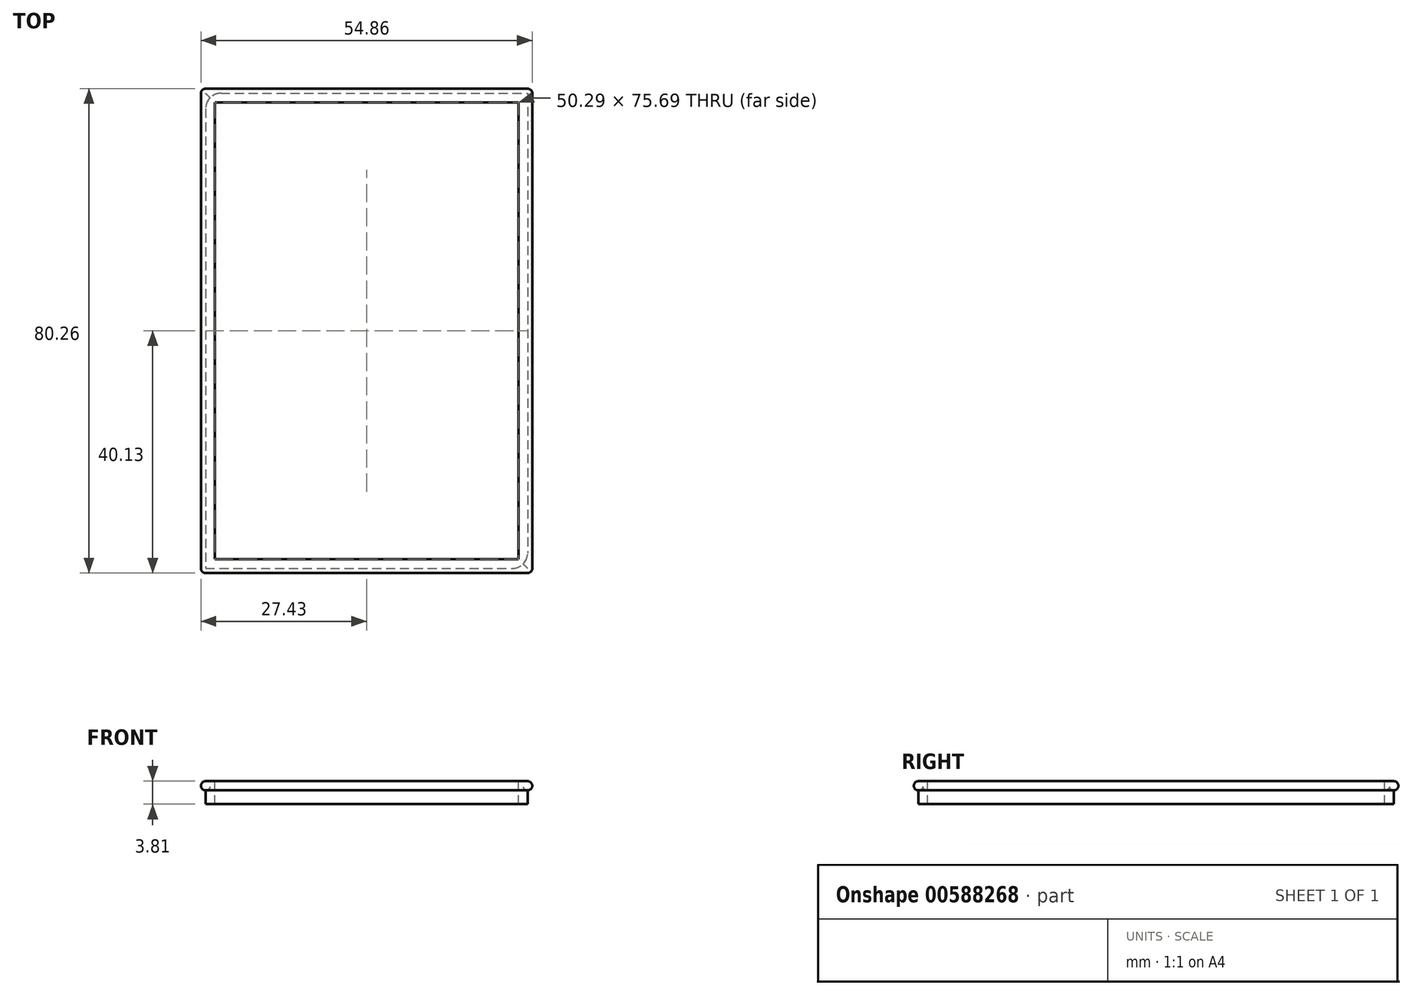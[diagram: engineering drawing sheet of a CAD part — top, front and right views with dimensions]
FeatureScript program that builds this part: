
annotation { "Feature Type Name" : "Feature", "Feature Type Description" : "" }
export const myFeature = defineFeature(function(context is Context, id is Id, definition is map)
    precondition{}
    {
        {
            var Q0;
            Q0=qCreatedBy(makeId("Front.planeOp"),FACE);
            var sketch = newSketch(context, id + "F0", { "sketchPlane" : qUnion([Q0])});
            skLineSegment(sketch, "E0.bottom", {"start": v(26.67, -20.32) * mm, "end": v(-26.67, -20.32) * mm});
            skLineSegment(sketch, "E0.top", {"start": v(26.67, 20.32) * mm, "end": v(-26.67, 20.32) * mm});
            skLineSegment(sketch, "E0.left", {"start": v(26.67, -20.32) * mm, "end": v(26.67, 20.32) * mm});
            skLineSegment(sketch, "E0.right", {"start": v(-26.67, -20.32) * mm, "end": v(-26.67, 20.32) * mm});
            skPoint(sketch, "E0.middle", {"position": v(0, 0) * mm});
            skSolve(sketch);
        }
        {
            var Q0;
            Q0=makeQuery(id+"F0.imprint","IMPRINT",FACE,{"disambiguationData":[TD([[makeQuery(id+"F0.imprint","IMPRINT",EDGE,{"derivedFrom":sQuery(id+"F0.wireOp",EDGE,"E0.bottom")}),-1.0]])]});
            extrude(context, id + "F1", {"entities" : qUnion([Q0]), "endBound" : BoundingType.SYMMETRIC, "depth" : 78.74 * mm});
        }
        {
            var Q0;
            Q0=makeQuery(id+"F1.opExtrude","SWEPT_FACE",FACE,{"disambiguationData":[OSD([sQuery(id+"F0.wireOp",EDGE,"E0.top")])]});
            shell(context, id + "F2", {"entities" : qUnion([Q0]), "thickness" : 1.52 * mm});
        }
        {
            var Q0;
            Q0=makeQuery(id+"F1.opExtrude","CAP_FACE",FACE,{"disambiguationData":[OSD([sQuery(id+"F0.wireOp",EDGE,"E0.bottom"),sQuery(id+"F0.wireOp",EDGE,"E0.top"),sQuery(id+"F0.wireOp",EDGE,"E0.left"),sQuery(id+"F0.wireOp",EDGE,"E0.right")])],"isStart":false});
            var sketch = newSketch(context, id + "F3", { "sketchPlane" : qUnion([Q0])});
            skArc(sketch, "E1", {"start": v(-26.67, 20.32) * mm, "mid": v(-27.43, 19.56) * mm, "end": v(-26.67, 18.8) * mm});
            skSolve(sketch);
        }
        {
            var Q0;
            {var subQ0=sQuery(id+"F3.wireOp",EDGE,"E1");Q0=makeQuery(id+"F3.imprint","IMPRINT",FACE,{"disambiguationData":[TD([[makeQuery(id+"F3.imprint","IMPRINT",EDGE,{"derivedFrom":subQ0}),1.0]])]});}
            var Q1;
            Q1=makeQuery(id+"F1.opExtrude","SWEPT_EDGE",EDGE,{"disambiguationData":[OSD([sQuery(id+"F0.wireOp",EDGE,"E0.top"),sQuery(id+"F0.wireOp",EDGE,"E0.right")])]});
            var Q2;
            Q2=makeQuery(id+"F1.opExtrude","CAP_EDGE",EDGE,{"disambiguationData":[OSD([sQuery(id+"F0.wireOp",EDGE,"E0.top")])],"isStart":true});
            var Q3;
            Q3=makeQuery(id+"F1.opExtrude","SWEPT_EDGE",EDGE,{"disambiguationData":[OSD([sQuery(id+"F0.wireOp",EDGE,"E0.top"),sQuery(id+"F0.wireOp",EDGE,"E0.left")])]});
            var Q4;
            Q4=makeQuery(id+"F1.opExtrude","CAP_EDGE",EDGE,{"disambiguationData":[OSD([sQuery(id+"F0.wireOp",EDGE,"E0.top")])],"isStart":false});
            sweep(context, id + "F4", {"operationType" : NewBodyOperationType.ADD, "profiles" : qUnion([Q0]), "path" : qUnion([Q1, Q2, Q3, Q4])});
        }
        {
            var Q0;
            Q0=makeQuery(id+"F1.opExtrude","SWEPT_FACE",FACE,{"disambiguationData":[OSD([sQuery(id+"F0.wireOp",EDGE,"E0.bottom")])]});
            var sketch = newSketch(context, id + "F5", { "sketchPlane" : qUnion([Q0])});
            skLineSegment(sketch, "E2.bottom", {"start": v(26.67, 39.37) * mm, "end": v(21.75, 39.37) * mm});
            skLineSegment(sketch, "E2.left", {"start": v(26.67, 39.37) * mm, "end": v(26.67, 34.45) * mm});
            skPoint(sketch, "E3.newPointA", {"position": v(20.32, 19.05) * mm});
            skArc(sketch, "E4", {"start": v(20.52, 37.78) * mm, "mid": v(22.18, 34.88) * mm, "end": v(25.08, 33.22) * mm});
            skPoint(sketch, "E5.visualSharp", {"position": v(20.32, 39.37) * mm});
            skArc(sketch, "E5.filletArc", {"start": v(21.75, 39.37) * mm, "mid": v(20.75, 38.88) * mm, "end": v(20.52, 37.78) * mm});
            skPoint(sketch, "E6.visualSharp", {"position": v(26.67, 33.02) * mm});
            skArc(sketch, "E6.filletArc", {"start": v(25.08, 33.22) * mm, "mid": v(26.18, 33.45) * mm, "end": v(26.67, 34.45) * mm});
            skArc(sketch, "E7.MirrorCS", {"start": v(-21.75, 39.37) * mm, "mid": v(-20.75, 38.88) * mm, "end": v(-20.52, 37.78) * mm});
            skArc(sketch, "E8.MirrorCS", {"start": v(-20.52, 37.78) * mm, "mid": v(-22.18, 34.88) * mm, "end": v(-25.08, 33.22) * mm});
            skArc(sketch, "E9.MirrorCS", {"start": v(-25.08, 33.22) * mm, "mid": v(-26.18, 33.45) * mm, "end": v(-26.67, 34.45) * mm});
            skLineSegment(sketch, "E10.MirrorCS", {"start": v(-26.67, 39.37) * mm, "end": v(-26.67, 34.45) * mm});
            skLineSegment(sketch, "E11.MirrorCS", {"start": v(-26.67, 39.37) * mm, "end": v(-21.75, 39.37) * mm});
            skArc(sketch, "E12.MirrorCS", {"start": v(-20.52, -37.78) * mm, "mid": v(-22.18, -34.88) * mm, "end": v(-25.08, -33.22) * mm});
            skArc(sketch, "E13.MirrorCS", {"start": v(-21.75, -39.37) * mm, "mid": v(-20.75, -38.88) * mm, "end": v(-20.52, -37.78) * mm});
            skLineSegment(sketch, "E14.MirrorCS", {"start": v(-26.67, -39.37) * mm, "end": v(-21.75, -39.37) * mm});
            skLineSegment(sketch, "E15.MirrorCS", {"start": v(-26.67, -39.37) * mm, "end": v(-26.67, -34.45) * mm});
            skArc(sketch, "E16.MirrorCS", {"start": v(-25.08, -33.22) * mm, "mid": v(-26.18, -33.45) * mm, "end": v(-26.67, -34.45) * mm});
            skArc(sketch, "E17.MirrorCS", {"start": v(21.75, -39.37) * mm, "mid": v(20.75, -38.88) * mm, "end": v(20.52, -37.78) * mm});
            skArc(sketch, "E18.MirrorCS", {"start": v(20.52, -37.78) * mm, "mid": v(22.18, -34.88) * mm, "end": v(25.08, -33.22) * mm});
            skArc(sketch, "E19.MirrorCS", {"start": v(25.08, -33.22) * mm, "mid": v(26.18, -33.45) * mm, "end": v(26.67, -34.45) * mm});
            skLineSegment(sketch, "E20.MirrorCS", {"start": v(26.67, -39.37) * mm, "end": v(26.67, -34.45) * mm});
            skLineSegment(sketch, "E21.MirrorCS", {"start": v(26.67, -39.37) * mm, "end": v(21.75, -39.37) * mm});
            skSolve(sketch);
        }
        {
            var Q0;
            Q0=makeQuery(id+"F5.imprint","IMPRINT",FACE,{"disambiguationData":[TD([[makeQuery(id+"F5.imprint","IMPRINT",EDGE,{"derivedFrom":sQuery(id+"F5.wireOp",EDGE,"E2.bottom")}),1.0]])]});
            var Q1;
            Q1=makeQuery(id+"F5.imprint","IMPRINT",FACE,{"disambiguationData":[TD([[makeQuery(id+"F5.imprint","IMPRINT",EDGE,{"derivedFrom":sQuery(id+"F5.wireOp",EDGE,"E8.MirrorCS")}),-1.0]])]});
            var Q2;
            Q2=makeQuery(id+"F5.imprint","IMPRINT",FACE,{"disambiguationData":[TD([[makeQuery(id+"F5.imprint","IMPRINT",EDGE,{"derivedFrom":sQuery(id+"F5.wireOp",EDGE,"E12.MirrorCS")}),1.0]])]});
            var Q3;
            Q3=makeQuery(id+"F5.imprint","IMPRINT",FACE,{"disambiguationData":[TD([[makeQuery(id+"F5.imprint","IMPRINT",EDGE,{"derivedFrom":sQuery(id+"F5.wireOp",EDGE,"E17.MirrorCS")}),-1.0]])]});
            extrude(context, id + "F6", {"entities" : qUnion([Q0, Q1, Q2, Q3]), "operationType" : NewBodyOperationType.ADD, "depth" : 2.8 * mm});
        }
        {
            var Q0;
            Q0=makeQuery(id+"F6.opExtrude","CAP_FACE",FACE,{"disambiguationData":[OSD([sQuery(id+"F5.wireOp",EDGE,"E2.bottom"),sQuery(id+"F5.wireOp",EDGE,"E2.left"),sQuery(id+"F5.wireOp",EDGE,"E4"),sQuery(id+"F5.wireOp",EDGE,"E5.filletArc"),sQuery(id+"F5.wireOp",EDGE,"E6.filletArc")])],"isStart":false});
            var Q1;
            Q1=makeQuery(id+"F6.opExtrude","CAP_FACE",FACE,{"disambiguationData":[OSD([sQuery(id+"F5.wireOp",EDGE,"E8.MirrorCS"),sQuery(id+"F5.wireOp",EDGE,"E9.MirrorCS"),sQuery(id+"F5.wireOp",EDGE,"E10.MirrorCS"),sQuery(id+"F5.wireOp",EDGE,"E7.MirrorCS"),sQuery(id+"F5.wireOp",EDGE,"E11.MirrorCS")])],"isStart":false});
            var Q2;
            Q2=makeQuery(id+"F6.opExtrude","CAP_FACE",FACE,{"disambiguationData":[OSD([sQuery(id+"F5.wireOp",EDGE,"E12.MirrorCS"),sQuery(id+"F5.wireOp",EDGE,"E13.MirrorCS"),sQuery(id+"F5.wireOp",EDGE,"E14.MirrorCS"),sQuery(id+"F5.wireOp",EDGE,"E15.MirrorCS"),sQuery(id+"F5.wireOp",EDGE,"E16.MirrorCS")])],"isStart":false});
            var Q3;
            Q3=makeQuery(id+"F6.opExtrude","CAP_FACE",FACE,{"disambiguationData":[OSD([sQuery(id+"F5.wireOp",EDGE,"E17.MirrorCS"),sQuery(id+"F5.wireOp",EDGE,"E18.MirrorCS"),sQuery(id+"F5.wireOp",EDGE,"E19.MirrorCS"),sQuery(id+"F5.wireOp",EDGE,"E20.MirrorCS"),sQuery(id+"F5.wireOp",EDGE,"E21.MirrorCS")])],"isStart":false});
            shell(context, id + "F7", {"entities" : qUnion([Q0, Q1, Q2, Q3]), "thickness" : 1.52 * mm});
        }
        {
            var Q0;
            Q0=makeQuery(id+"F2.opShell","OFFSET_FACE",FACE,{"disambiguationData":[OSD([sQuery(id+"F0.wireOp",EDGE,"E0.bottom")])]});
            fillet(context, id + "F8", {"entities" : qUnion([Q0]), "radius" : 0.76 * mm, "tangentPropagation" : true, "allowEdgeOverflow" : false});
        }
        {
            var Q0;
            Q0=makeQuery(id+"F1.opExtrude","SWEPT_EDGE",EDGE,{"disambiguationData":[OSD([sQuery(id+"F0.wireOp",EDGE,"E0.bottom"),sQuery(id+"F0.wireOp",EDGE,"E0.right")])]});
            var Q1;
            Q1=makeQuery(id+"F1.opExtrude","CAP_EDGE",EDGE,{"disambiguationData":[OSD([sQuery(id+"F0.wireOp",EDGE,"E0.bottom")])],"isStart":false});
            var Q2;
            Q2=makeQuery(id+"F1.opExtrude","SWEPT_EDGE",EDGE,{"disambiguationData":[OSD([sQuery(id+"F0.wireOp",EDGE,"E0.bottom"),sQuery(id+"F0.wireOp",EDGE,"E0.left")])]});
            var Q3;
            Q3=makeQuery(id+"F1.opExtrude","CAP_EDGE",EDGE,{"disambiguationData":[OSD([sQuery(id+"F0.wireOp",EDGE,"E0.bottom")])],"isStart":true});
            fillet(context, id + "F9", {"entities" : qUnion([Q0, Q1, Q2, Q3]), "radius" : 1.9 * mm, "tangentPropagation" : true, "allowEdgeOverflow" : false});
        }
        {
            var Q0;
            Q0=makeQuery(id+"F4.opSweep","MID_CAP_EDGE",EDGE,{"disambiguationData":[OSD([sQuery(id+"F0.wireOp",EDGE,"E0.top"),sQuery(id+"F0.wireOp",EDGE,"E0.left"),sQuery(id+"F3.wireOp",EDGE,"E1")])],"capPos":3.0});
            var Q1;
            Q1=makeQuery(id+"F4.opSweep","MID_CAP_EDGE",EDGE,{"disambiguationData":[OSD([sQuery(id+"F0.wireOp",EDGE,"E0.top"),sQuery(id+"F0.wireOp",EDGE,"E0.left"),sQuery(id+"F3.wireOp",EDGE,"E1")])],"capPos":2.0});
            var Q2;
            Q2=makeQuery(id+"F4.opSweep","MID_CAP_EDGE",EDGE,{"disambiguationData":[OSD([sQuery(id+"F0.wireOp",EDGE,"E0.top"),sQuery(id+"F0.wireOp",EDGE,"E0.right"),sQuery(id+"F3.wireOp",EDGE,"E1")])],"capPos":1.0});
            var Q3;
            Q3=makeQuery(id+"F4.opSweep","CAP_EDGE",EDGE,{"disambiguationData":[OSD([sQuery(id+"F0.wireOp",EDGE,"E0.top"),sQuery(id+"F0.wireOp",EDGE,"E0.right"),sQuery(id+"F3.wireOp",EDGE,"E1")])],"isStart":true});
            fillet(context, id + "F10", {"entities" : qUnion([Q0, Q1, Q2, Q3]), "radius" : 0.76 * mm, "tangentPropagation" : true, "allowEdgeOverflow" : false});
        }
        {
            var Q0;
            Q0=makeQuery(id+"F6.boolean.opBoolean","MERGE",EDGE,{"derivedFrom":[makeQuery(id+"F1.opExtrude","CAP_EDGE",EDGE,{"disambiguationData":[OSD([sQuery(id+"F0.wireOp",EDGE,"E0.left")])],"isStart":false}),makeQuery(id+"F6.opExtrude","SWEPT_EDGE",EDGE,{"disambiguationData":[OSD([sQuery(id+"F5.wireOp",EDGE,"E2.bottom"),sQuery(id+"F5.wireOp",EDGE,"E2.left")])]})]});
            var Q1;
            Q1=makeQuery(id+"F6.boolean.opBoolean","MERGE",EDGE,{"derivedFrom":[makeQuery(id+"F1.opExtrude","CAP_EDGE",EDGE,{"disambiguationData":[OSD([sQuery(id+"F0.wireOp",EDGE,"E0.left")])],"isStart":true}),makeQuery(id+"F6.opExtrude","SWEPT_EDGE",EDGE,{"disambiguationData":[OSD([sQuery(id+"F5.wireOp",EDGE,"E20.MirrorCS"),sQuery(id+"F5.wireOp",EDGE,"E21.MirrorCS")])]})]});
            var Q2;
            Q2=makeQuery(id+"F6.boolean.opBoolean","MERGE",EDGE,{"derivedFrom":[makeQuery(id+"F1.opExtrude","CAP_EDGE",EDGE,{"disambiguationData":[OSD([sQuery(id+"F0.wireOp",EDGE,"E0.right")])],"isStart":false}),makeQuery(id+"F6.opExtrude","SWEPT_EDGE",EDGE,{"disambiguationData":[OSD([sQuery(id+"F5.wireOp",EDGE,"E10.MirrorCS"),sQuery(id+"F5.wireOp",EDGE,"E11.MirrorCS")])]})]});
            var Q3;
            Q3=makeQuery(id+"F6.boolean.opBoolean","MERGE",EDGE,{"derivedFrom":[makeQuery(id+"F1.opExtrude","CAP_EDGE",EDGE,{"disambiguationData":[OSD([sQuery(id+"F0.wireOp",EDGE,"E0.right")])],"isStart":true}),makeQuery(id+"F6.opExtrude","SWEPT_EDGE",EDGE,{"disambiguationData":[OSD([sQuery(id+"F5.wireOp",EDGE,"E14.MirrorCS"),sQuery(id+"F5.wireOp",EDGE,"E15.MirrorCS")])]})]});
            fillet(context, id + "F11", {"entities" : qUnion([Q0, Q1, Q2, Q3]), "radius" : 2.54 * mm, "tangentPropagation" : true, "allowEdgeOverflow" : false});
        }
        {
            var Q0;
            Q0=makeQuery(id+"F1.opExtrude","SWEPT_BODY",BODY,{"disambiguationData":[OSD([sQuery(id+"F0.wireOp",EDGE,"E0.bottom"),sQuery(id+"F0.wireOp",EDGE,"E0.top"),sQuery(id+"F0.wireOp",EDGE,"E0.left"),sQuery(id+"F0.wireOp",EDGE,"E0.right")])]});
            transform(context, id + "F12", {"entities" : qUnion([Q0]), "transformType" : TransformType.COPY});
        }
        {
            var Q0;
            Q0=makeQuery(id+"F12.opPattern","COPY",BODY,{"derivedFrom":makeQuery(id+"F1.opExtrude","SWEPT_BODY",BODY,{"disambiguationData":[OSD([sQuery(id+"F0.wireOp",EDGE,"E0.bottom"),sQuery(id+"F0.wireOp",EDGE,"E0.top"),sQuery(id+"F0.wireOp",EDGE,"E0.left"),sQuery(id+"F0.wireOp",EDGE,"E0.right")])]}),"instanceName":"1"});
            deleteBodies(context, id + "F13", {"entities" : qUnion([Q0])});
        }
        {
            var Q0;
            Q0=makeQuery(id+"F1.opExtrude","SWEPT_FACE",FACE,{"disambiguationData":[OSD([sQuery(id+"F0.wireOp",EDGE,"E0.bottom")])]});
            var sketch = newSketch(context, id + "F14", { "sketchPlane" : qUnion([Q0])});
            skLineSegment(sketch, "E22.bottom", {"start": v(32.2, -45.45) * mm, "end": v(-32.2, -45.45) * mm});
            skLineSegment(sketch, "E22.top", {"start": v(32.2, 45.45) * mm, "end": v(-32.2, 45.45) * mm});
            skLineSegment(sketch, "E22.left", {"start": v(32.2, -45.45) * mm, "end": v(32.2, 45.45) * mm});
            skLineSegment(sketch, "E22.right", {"start": v(-32.2, -45.45) * mm, "end": v(-32.2, 45.45) * mm});
            skPoint(sketch, "E22.middle", {"position": v(0, 0) * mm});
            skSolve(sketch);
        }
        {
            var Q0;
            Q0 = qSketchRegion(id + "F14", true);
            extrude(context, id + "F15", {"entities" : qUnion([Q0]), "operationType" : NewBodyOperationType.REMOVE, "endBound" : BoundingType.SYMMETRIC, "oppositeDirection" : true, "depth" : 73.66 * mm, "offsetDistance" : 25.4 * mm});
        }
    });
